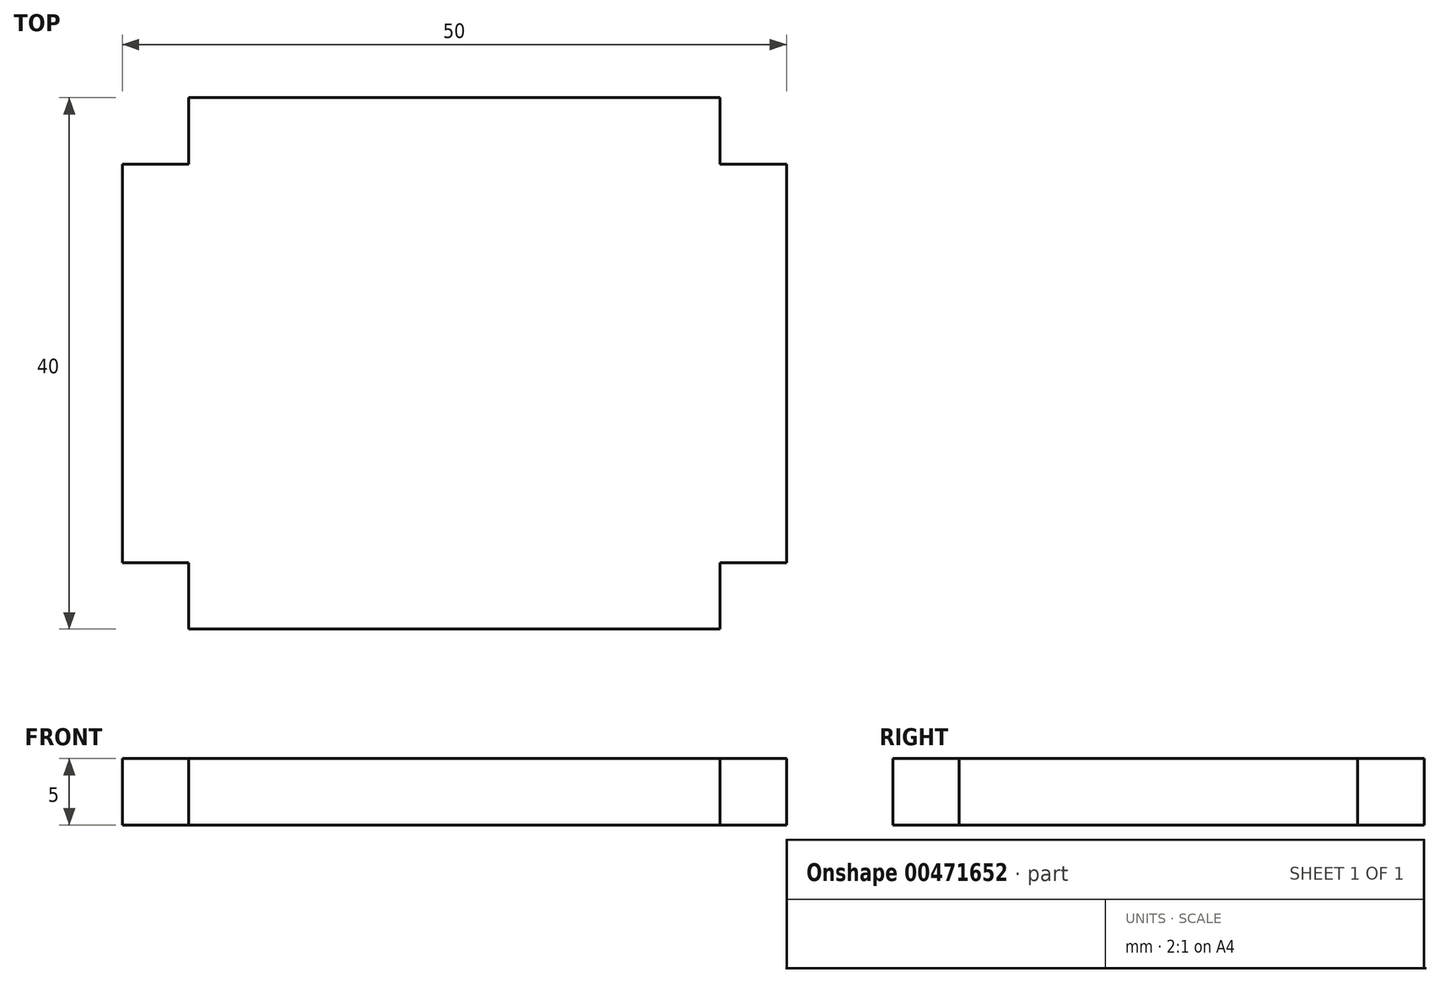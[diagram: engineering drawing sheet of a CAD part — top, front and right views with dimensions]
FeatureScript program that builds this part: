
annotation { "Feature Type Name" : "Feature", "Feature Type Description" : "" }
export const myFeature = defineFeature(function(context is Context, id is Id, definition is map)
    precondition{}
    {
        {
            var Q0;
            Q0=qCreatedBy(makeId("Top.planeOp"),FACE);
            var sketch = newSketch(context, id + "F0", { "sketchPlane" : qUnion([Q0])});
            skLineSegment(sketch, "E0.bottom", {"start": v(-18.76, 19.1) * mm, "end": v(21.24, 19.1) * mm});
            skLineSegment(sketch, "E0.top", {"start": v(-18.76, -20.9) * mm, "end": v(21.24, -20.9) * mm});
            skLineSegment(sketch, "E0.left", {"start": v(-23.76, 14.1) * mm, "end": v(-23.76, -15.9) * mm});
            skLineSegment(sketch, "E0.right", {"start": v(26.24, 14.1) * mm, "end": v(26.24, -15.9) * mm});
            skLineSegment(sketch, "E1", {"start": v(-23.76, 14.1) * mm, "end": v(-18.76, 14.1) * mm});
            skLineSegment(sketch, "E2", {"start": v(-18.76, 14.1) * mm, "end": v(-18.76, 19.1) * mm});
            skLineSegment(sketch, "E3", {"start": v(21.24, 19.1) * mm, "end": v(21.24, 14.1) * mm});
            skLineSegment(sketch, "E4", {"start": v(21.24, 14.1) * mm, "end": v(26.24, 14.1) * mm});
            skLineSegment(sketch, "E5", {"start": v(-23.76, -15.9) * mm, "end": v(-18.76, -15.9) * mm});
            skLineSegment(sketch, "E6", {"start": v(-18.76, -15.9) * mm, "end": v(-18.76, -20.9) * mm});
            skLineSegment(sketch, "E7", {"start": v(21.24, -20.9) * mm, "end": v(21.24, -15.9) * mm});
            skLineSegment(sketch, "E8", {"start": v(21.24, -15.9) * mm, "end": v(26.24, -15.9) * mm});
            skSolve(sketch);
        }
        {
            var Q0;
            Q0=makeQuery(id+"F0.imprint","IMPRINT",FACE,{"disambiguationData":[TD([[makeQuery(id+"F0.imprint","IMPRINT",EDGE,{"derivedFrom":sQuery(id+"F0.wireOp",EDGE,"E0.bottom")}),-1.0]])]});
            extrude(context, id + "F1", {"entities" : qUnion([Q0]), "depth" : 5 * mm});
        }
    });
